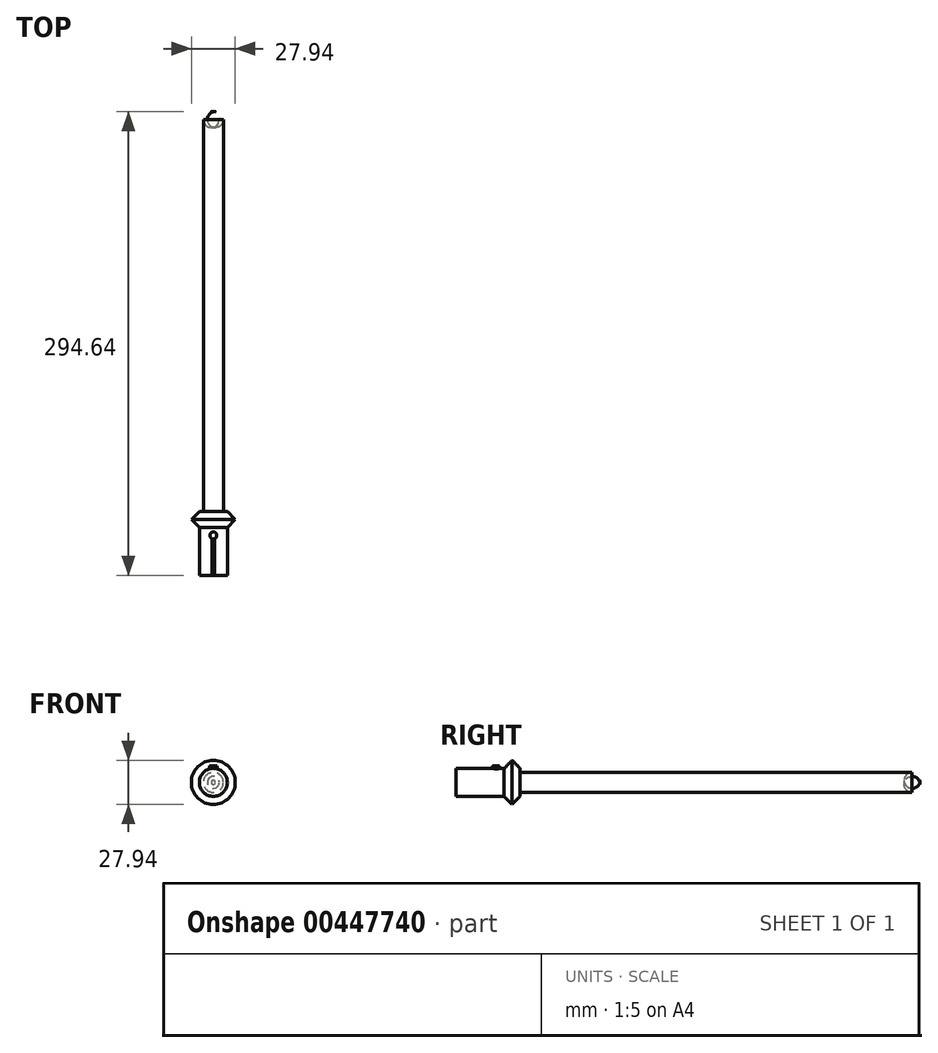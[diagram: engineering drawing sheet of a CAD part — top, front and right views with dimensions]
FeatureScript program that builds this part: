
annotation { "Feature Type Name" : "Feature", "Feature Type Description" : "" }
export const myFeature = defineFeature(function(context is Context, id is Id, definition is map)
    precondition{}
    {
        {
            var Q0;
            Q0=qCreatedBy(makeId("Top.planeOp"),FACE);
            var sketch = newSketch(context, id + "F0", { "sketchPlane" : qUnion([Q0])});
            skLineSegment(sketch, "E0", {"start": v(0, 40.64) * mm, "end": v(0, 0) * mm, "construction": true});
            skLineSegment(sketch, "E1", {"start": v(0, 0) * mm, "end": v(8.9, 0) * mm});
            skLineSegment(sketch, "E2", {"start": v(8.9, 0) * mm, "end": v(8.9, 30.48) * mm});
            skLineSegment(sketch, "E3", {"start": v(8.9, 30.48) * mm, "end": v(13.97, 35.56) * mm});
            skLineSegment(sketch, "E4", {"start": v(13.97, 35.56) * mm, "end": v(8.9, 40.64) * mm});
            skLineSegment(sketch, "E5", {"start": v(8.9, 40.64) * mm, "end": v(0, 40.64) * mm});
            skLineSegment(sketch, "E6.trimOffspring", {"start": v(0, 40.64) * mm, "end": v(0, 0) * mm});
            skSolve(sketch);
        }
        {
            var Q0;
            Q0 = qSketchRegion(id + "F0", true);
            var Q1;
            Q1=sQuery(id+"F0.wireOp",EDGE,"E6.trimOffspring");
            revolve(context, id + "F1", {"entities" : qUnion([Q0]), "axis" : qUnion([Q1]), "revolveType" : RevolveType.FULL});
        }
        {
            var Q0;
            Q0=qCreatedBy(makeId("Top.planeOp"),FACE);
            var sketch = newSketch(context, id + "F2", { "sketchPlane" : qUnion([Q0])});
            skLineSegment(sketch, "E7", {"start": v(0, 40.64) * mm, "end": v(0, 72.8) * mm, "construction": true});
            skLineSegment(sketch, "E8.bottom", {"start": v(0, 40.64) * mm, "end": v(6.35, 40.64) * mm});
            skLineSegment(sketch, "E8.top", {"start": v(0, 294.64) * mm, "end": v(6.35, 294.64) * mm});
            skLineSegment(sketch, "E8.left", {"start": v(0, 40.64) * mm, "end": v(0, 294.64) * mm});
            skLineSegment(sketch, "E8.right", {"start": v(6.35, 40.64) * mm, "end": v(6.35, 294.64) * mm});
            skSolve(sketch);
        }
        {
            var Q0;
            Q0 = qSketchRegion(id + "F2", true);
            var Q1;
            Q1=sQuery(id+"F2.wireOp",EDGE,"E8.left");
            revolve(context, id + "F3", {"entities" : qUnion([Q0]), "axis" : qUnion([Q1]), "revolveType" : RevolveType.FULL});
        }
        {
            var Q0;
            Q0=makeQuery(id+"F3.opRevolve","SWEPT_EDGE",EDGE,{"disambiguationData":[OSD([sQuery(id+"F2.wireOp",EDGE,"E8.top"),sQuery(id+"F2.wireOp",EDGE,"E8.right")])]});
            fillet(context, id + "F4", {"entities" : qUnion([Q0]), "radius" : 5.08 * mm, "tangentPropagation" : true, "allowEdgeOverflow" : false});
        }
        {
            var Q0;
            Q0=makeQuery(id+"F1.opRevolve","SWEPT_FACE",FACE,{"disambiguationData":[OSD([sQuery(id+"F0.wireOp",EDGE,"E1")])]});
            var sketch = newSketch(context, id + "F5", { "sketchPlane" : qUnion([Q0])});
            skLineSegment(sketch, "E9", {"start": v(-2.03, 10.16) * mm, "end": v(0, 8.13) * mm});
            skLineSegment(sketch, "E10", {"start": v(0, 8.13) * mm, "end": v(2.03, 10.16) * mm});
            skLineSegment(sketch, "E11", {"start": v(-2.03, 10.16) * mm, "end": v(2.03, 10.16) * mm});
            skLineSegment(sketch, "E12", {"start": v(0, 8.13) * mm, "end": v(0, 10.16) * mm, "construction": true});
            skSolve(sketch);
        }
        {
            var Q0;
            Q0 = qSketchRegion(id + "F5", true);
            extrude(context, id + "F6", {"entities" : qUnion([Q0]), "operationType" : NewBodyOperationType.REMOVE, "oppositeDirection" : true, "depth" : 25.4 * mm});
        }
        {
            var Q0;
            Q0=qCreatedBy(makeId("Top.planeOp"),FACE);
            var sketch = newSketch(context, id + "F7", { "sketchPlane" : qUnion([Q0])});
            skLineSegment(sketch, "E13", {"start": v(0, 0) * mm, "end": v(0, 20.48) * mm, "construction": true});
            skCircle(sketch, "E14", {"center": v(0, 25.4) * mm, "radius": 2.22 * mm});
            skSolve(sketch);
        }
        {
            var Q0;
            Q0 = qSketchRegion(id + "F7", true);
            extrude(context, id + "F8", {"entities" : qUnion([Q0]), "operationType" : NewBodyOperationType.ADD, "depth" : 10.4 * mm});
        }
    });
